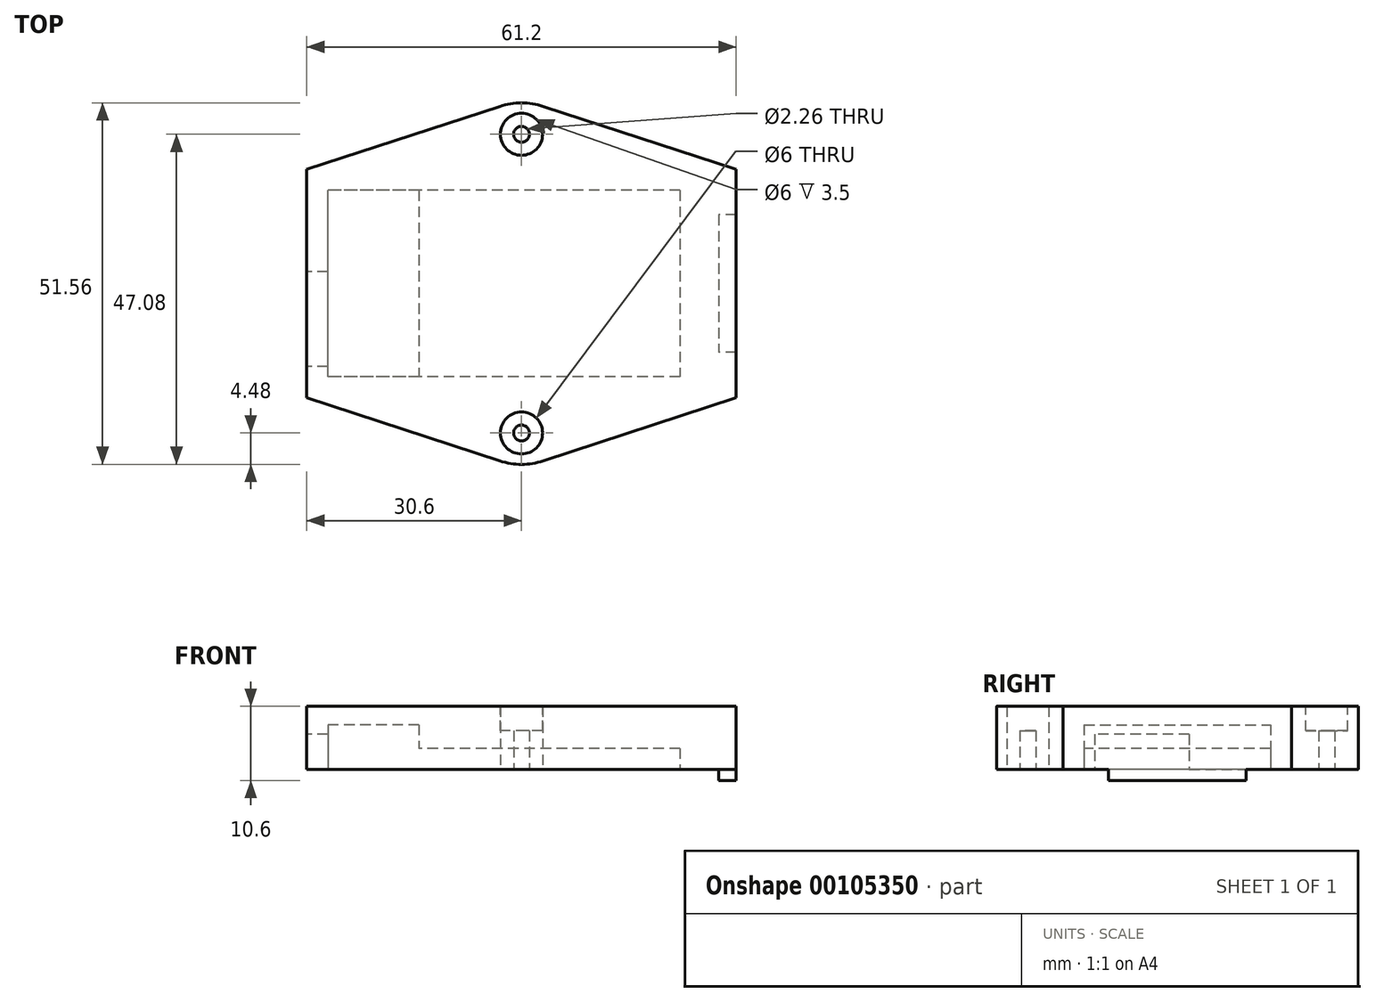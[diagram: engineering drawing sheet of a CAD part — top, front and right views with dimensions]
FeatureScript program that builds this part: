
annotation { "Feature Type Name" : "Feature", "Feature Type Description" : "" }
export const myFeature = defineFeature(function(context is Context, id is Id, definition is map)
    precondition{}
    {
        {
            var Q0;
            Q0=qCreatedBy(makeId("Top.planeOp"),FACE);
            cPlane(context, id + "F0", {"entities" : qUnion([Q0]), "cplaneType" : CPlaneType.OFFSET, "offset" : 18.75 * mm, "width" : 150 * mm, "height" : 150 * mm});
        }
        {
            var Q0;
            Q0=qCreatedBy(id+"F0.planeOp",FACE);
            var sketch = newSketch(context, id + "F1", { "sketchPlane" : qUnion([Q0])});
            skLineSegment(sketch, "E0.bottom", {"start": v(27.6, -13.3) * mm, "end": v(-27.6, -13.3) * mm});
            skLineSegment(sketch, "E0.top", {"start": v(27.6, 13.3) * mm, "end": v(-27.6, 13.3) * mm});
            skLineSegment(sketch, "E0.left", {"start": v(27.6, -13.3) * mm, "end": v(27.6, 13.3) * mm});
            skLineSegment(sketch, "E0.right", {"start": v(-27.6, -13.3) * mm, "end": v(-27.6, 13.3) * mm});
            skPoint(sketch, "E0.middle", {"position": v(0, 0) * mm});
            skLineSegment(sketch, "E1.bottom", {"start": v(30.6, 16.3) * mm, "end": v(-30.6, 16.3) * mm});
            skLineSegment(sketch, "E1.top", {"start": v(30.6, -16.3) * mm, "end": v(-30.6, -16.3) * mm});
            skLineSegment(sketch, "E1.left", {"start": v(30.6, 16.3) * mm, "end": v(30.6, -16.3) * mm});
            skLineSegment(sketch, "E1.right", {"start": v(-30.6, 16.3) * mm, "end": v(-30.6, -16.3) * mm});
            skLineSegment(sketch, "E2", {"start": v(-602, 0) * mm, "end": v(-602, 0) * mm});
            skPoint(sketch, "E2.endSnap0", {"position": v(30.6, 0) * mm});
            skPoint(sketch, "E3.middle", {"position": v(-1.1, 0) * mm});
            skLineSegment(sketch, "E4", {"start": v(-24.31, 0) * mm, "end": v(42.86, 0) * mm, "construction": true});
            skLineSegment(sketch, "E5", {"start": v(22.6, 13.3) * mm, "end": v(22.6, 10.3) * mm});
            skLineSegment(sketch, "E6.MirrorCS", {"start": v(22.6, -13.3) * mm, "end": v(22.6, -10.3) * mm});
            skLineSegment(sketch, "E7", {"start": v(0, 27.42) * mm, "end": v(0, -25.6) * mm, "construction": true});
            skPoint(sketch, "E7.startSnap0", {"position": v(0, 13.3) * mm});
            skPoint(sketch, "E7.endSnap0", {"position": v(0, 16.3) * mm});
            skLineSegment(sketch, "E8", {"start": v(-30.6, 16.3) * mm, "end": v(-3.1, 25.28) * mm});
            skLineSegment(sketch, "E9", {"start": v(3.1, 25.28) * mm, "end": v(30.6, 16.3) * mm});
            skPoint(sketch, "E10.visualSharp", {"position": v(0, 26.3) * mm});
            skArc(sketch, "E10.filletArc", {"start": v(3.1, 25.28) * mm, "mid": v(0, 25.78) * mm, "end": v(-3.1, 25.28) * mm});
            skLineSegment(sketch, "E11.MirrorCS", {"start": v(-30.6, -16.3) * mm, "end": v(-3.1, -25.28) * mm});
            skLineSegment(sketch, "E12.MirrorCS", {"start": v(3.1, -25.28) * mm, "end": v(30.6, -16.3) * mm});
            skArc(sketch, "E13.MirrorCS", {"start": v(3.1, -25.28) * mm, "mid": v(0, -25.78) * mm, "end": v(-3.1, -25.28) * mm});
            skLineSegment(sketch, "E14", {"start": v(-27.6, 13.3) * mm, "end": v(-30.6, 13.3) * mm});
            skLineSegment(sketch, "E15", {"start": v(-27.6, -13.3) * mm, "end": v(-30.6, -13.3) * mm});
            skLineSegment(sketch, "E16", {"start": v(27.6, 10.3) * mm, "end": v(30.6, 10.3) * mm});
            skLineSegment(sketch, "E17", {"start": v(27.6, -10.3) * mm, "end": v(30.6, -10.3) * mm});
            skLineSegment(sketch, "E18", {"start": v(-27.6, 1.7) * mm, "end": v(-30.6, 1.7) * mm});
            skLineSegment(sketch, "E19", {"start": v(-27.6, -11.8) * mm, "end": v(-30.6, -11.8) * mm});
            skCircle(sketch, "E20", {"center": v(0, 21.3) * mm, "radius": 1.13 * mm});
            skCircle(sketch, "E21.MirrorC", {"center": v(0, -21.3) * mm, "radius": 1.13 * mm});
            skLineSegment(sketch, "E22", {"start": v(22.6, 10.3) * mm, "end": v(22.6, -10.3) * mm});
            skLineSegment(sketch, "E23", {"start": v(30.6, 9.8) * mm, "end": v(28.1, 9.8) * mm});
            skLineSegment(sketch, "E24", {"start": v(28.1, 9.8) * mm, "end": v(28.1, 0) * mm});
            skLineSegment(sketch, "E25.MirrorCS", {"start": v(28.1, -9.8) * mm, "end": v(28.1, 0) * mm});
            skLineSegment(sketch, "E26.MirrorCS", {"start": v(30.6, -9.8) * mm, "end": v(28.1, -9.8) * mm});
            skCircle(sketch, "E27", {"center": v(0, 21.3) * mm, "radius": 3 * mm});
            skCircle(sketch, "E28.MirrorC", {"center": v(0, -21.3) * mm, "radius": 3 * mm});
            skLineSegment(sketch, "E29", {"start": v(-14.6, 13.3) * mm, "end": v(-14.6, -13.3) * mm});
            skSolve(sketch);
        }
        {
            var Q0;
            {var subQ0=sQuery(id+"F1.wireOp",EDGE,"E23");Q0=makeQuery(id+"F1.imprint","IMPRINT",FACE,{"disambiguationData":[TD([[makeQuery(id+"F1.imprint","IMPRINT",EDGE,{"derivedFrom":subQ0}),1.0]])]});}
            extrude(context, id + "F2", {"entities" : qUnion([Q0]), "oppositeDirection" : true, "depth" : 1.6 * mm});
        }
        {
            var Q0;
            Q0 = qSketchRegion(id + "F1", true);
            var Q1;
            {var subQ7=sQuery(id+"F1.wireOp",EDGE,"E29");Q1=makeQuery(id+"F1.imprint","IMPRINT",FACE,{"disambiguationData":[TD([[makeQuery(id+"F1.imprint","IMPRINT",EDGE,{"derivedFrom":subQ7}),-1.0]])]});}
            var Q2;
            {var subQ1=sQuery(id+"F1.wireOp",EDGE,"E5");Q2=makeQuery(id+"F1.imprint","IMPRINT",FACE,{"disambiguationData":[TD([[makeQuery(id+"F1.imprint","IMPRINT",EDGE,{"derivedFrom":subQ1}),-1.0]])]});}
            var Q3;
            {var subQ6=sQuery(id+"F1.wireOp",EDGE,"E5");Q3=makeQuery(id+"F1.imprint","IMPRINT",FACE,{"disambiguationData":[TD([[makeQuery(id+"F1.imprint","IMPRINT",EDGE,{"derivedFrom":subQ6}),1.0]])]});}
            var Q4;
            Q4=makeQuery(id+"F1.imprint","IMPRINT",FACE,{"disambiguationData":[TD([[makeQuery(id+"F1.imprint","IMPRINT",EDGE,{"derivedFrom":sQuery(id+"F1.wireOp",EDGE,"E21.MirrorC")}),1.0]])]});
            var Q5;
            Q5=makeQuery(id+"F1.imprint","IMPRINT",FACE,{"disambiguationData":[TD([[makeQuery(id+"F1.imprint","IMPRINT",EDGE,{"derivedFrom":sQuery(id+"F1.wireOp",EDGE,"E20")}),-1.0]])]});
            extrude(context, id + "F3", {"entities" : qUnion([Q0, Q1, Q2, Q3, Q4, Q5]), "operationType" : NewBodyOperationType.ADD, "depth" : 9 * mm});
        }
        {
            var Q0;
            {var subQ1=sQuery(id+"F1.wireOp",EDGE,"E5");Q0=makeQuery(id+"F1.imprint","IMPRINT",FACE,{"disambiguationData":[TD([[makeQuery(id+"F1.imprint","IMPRINT",EDGE,{"derivedFrom":subQ1}),-1.0]])]});}
            extrude(context, id + "F4", {"entities" : qUnion([Q0]), "operationType" : NewBodyOperationType.REMOVE, "depth" : 3 * mm});
        }
        {
            var Q0;
            {var subQ0=sQuery(id+"F1.wireOp",EDGE,"E18");Q0=makeQuery(id+"F1.imprint","IMPRINT",FACE,{"disambiguationData":[TD([[makeQuery(id+"F1.imprint","IMPRINT",EDGE,{"derivedFrom":subQ0}),1.0]])]});}
            extrude(context, id + "F5", {"entities" : qUnion([Q0]), "operationType" : NewBodyOperationType.REMOVE, "depth" : 5 * mm});
        }
        {
            var Q0;
            {var subQ7=sQuery(id+"F1.wireOp",EDGE,"E29");Q0=makeQuery(id+"F1.imprint","IMPRINT",FACE,{"disambiguationData":[TD([[makeQuery(id+"F1.imprint","IMPRINT",EDGE,{"derivedFrom":subQ7}),-1.0]])]});}
            extrude(context, id + "F6", {"entities" : qUnion([Q0]), "operationType" : NewBodyOperationType.REMOVE, "depth" : 6.35 * mm});
        }
        {
            var Q0;
            Q0=makeQuery(id+"F3.opExtrude","CAP_FACE",FACE,{"disambiguationData":[OSD([sQuery(id+"F1.wireOp",EDGE,"E1.left"),sQuery(id+"F1.wireOp",EDGE,"E1.right"),sQuery(id+"F1.wireOp",EDGE,"E8"),sQuery(id+"F1.wireOp",EDGE,"E9"),sQuery(id+"F1.wireOp",EDGE,"E10.filletArc"),sQuery(id+"F1.wireOp",EDGE,"E11.MirrorCS"),sQuery(id+"F1.wireOp",EDGE,"E12.MirrorCS"),sQuery(id+"F1.wireOp",EDGE,"E13.MirrorCS"),sQuery(id+"F1.wireOp",EDGE,"E20"),sQuery(id+"F1.wireOp",EDGE,"E21.MirrorC")])],"isStart":false});
            var sketch = newSketch(context, id + "F7", { "sketchPlane" : qUnion([Q0])});
            skCircle(sketch, "E30", {"center": v(0, 21.3) * mm, "radius": 3 * mm});
            skCircle(sketch, "E31", {"center": v(0, -21.3) * mm, "radius": 3 * mm});
            skSolve(sketch);
        }
        {
            var Q0;
            Q0 = qSketchRegion(id + "F7", true);
            extrude(context, id + "F8", {"entities" : qUnion([Q0]), "operationType" : NewBodyOperationType.REMOVE, "oppositeDirection" : true, "depth" : 3.5 * mm});
        }
    });
